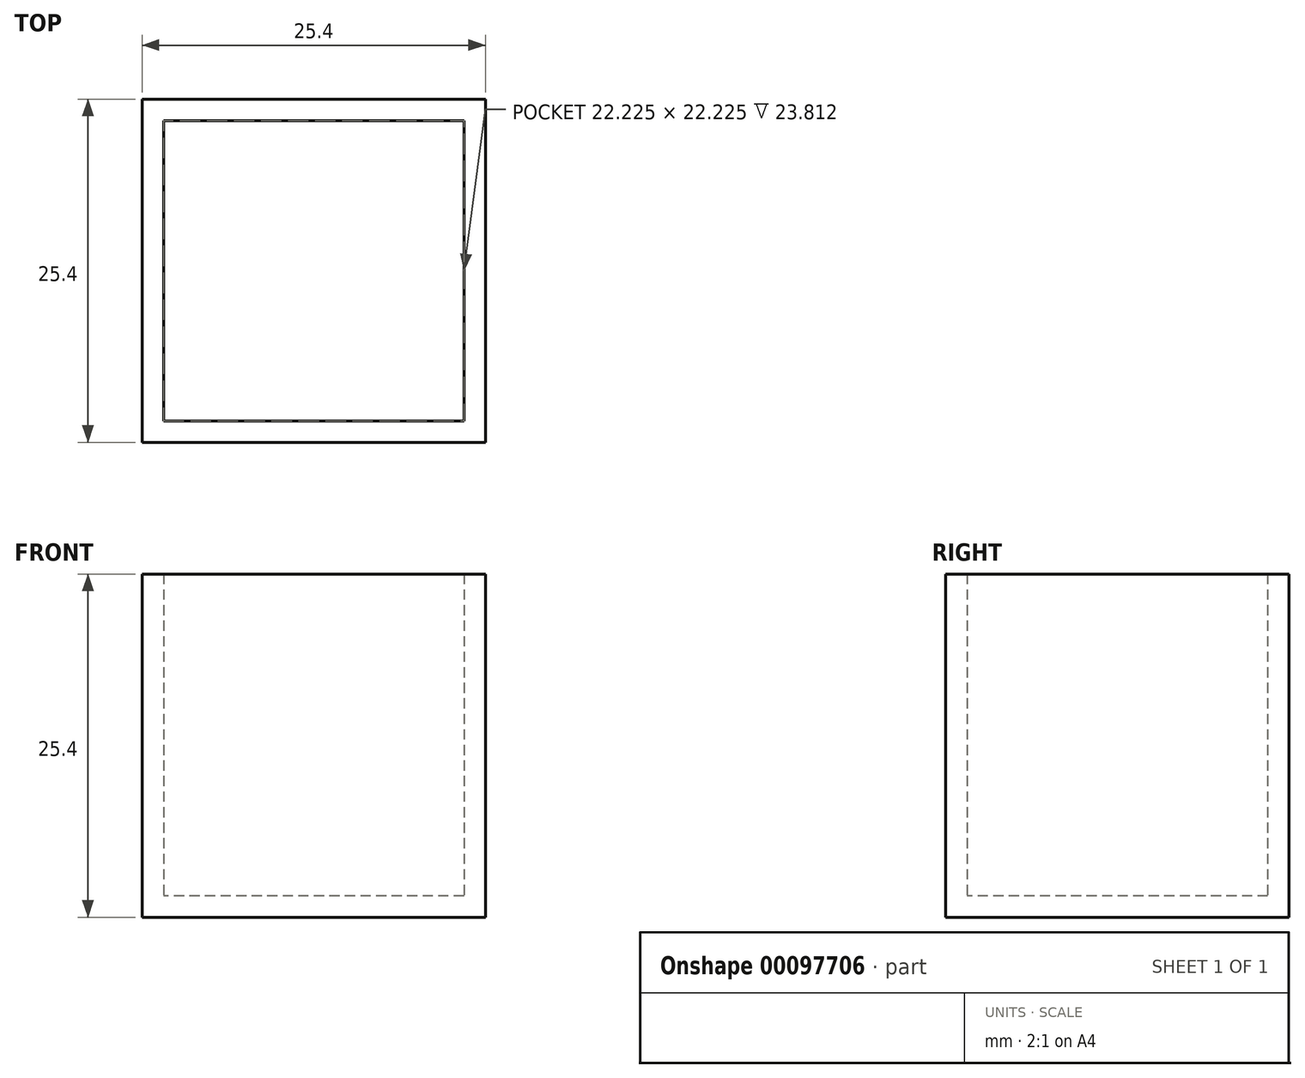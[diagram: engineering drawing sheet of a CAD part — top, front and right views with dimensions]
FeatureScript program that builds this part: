
annotation { "Feature Type Name" : "Feature", "Feature Type Description" : "" }
export const myFeature = defineFeature(function(context is Context, id is Id, definition is map)
    precondition{}
    {
        {
            var Q0;
            Q0=qCreatedBy(makeId("Top.planeOp"),FACE);
            var sketch = newSketch(context, id + "F0", { "sketchPlane" : qUnion([Q0])});
            skLineSegment(sketch, "E0.bottom", {"start": v(12.7, 12.7) * mm, "end": v(-12.7, 12.7) * mm});
            skLineSegment(sketch, "E0.top", {"start": v(12.7, -12.7) * mm, "end": v(-12.7, -12.7) * mm});
            skLineSegment(sketch, "E0.left", {"start": v(12.7, 12.7) * mm, "end": v(12.7, -12.7) * mm});
            skLineSegment(sketch, "E0.right", {"start": v(-12.7, 12.7) * mm, "end": v(-12.7, -12.7) * mm});
            skPoint(sketch, "E0.middle", {"position": v(0, 0) * mm});
            skSolve(sketch);
        }
        {
            var Q0;
            Q0 = qSketchRegion(id + "F0", true);
            extrude(context, id + "F1", {"entities" : qUnion([Q0]), "depth" : 1.59 * mm});
        }
        {
            var Q0;
            Q0=makeQuery(id+"F1.opExtrude","CAP_FACE",FACE,{"disambiguationData":[OSD([sQuery(id+"F0.wireOp",EDGE,"E0.bottom"),sQuery(id+"F0.wireOp",EDGE,"E0.top"),sQuery(id+"F0.wireOp",EDGE,"E0.left"),sQuery(id+"F0.wireOp",EDGE,"E0.right")])],"isStart":false});
            var sketch = newSketch(context, id + "F2", { "sketchPlane" : qUnion([Q0])});
            skLineSegment(sketch, "E1.bottom", {"start": v(11.11, 11.11) * mm, "end": v(-11.11, 11.11) * mm});
            skLineSegment(sketch, "E1.top", {"start": v(11.11, -11.11) * mm, "end": v(-11.11, -11.11) * mm});
            skLineSegment(sketch, "E1.left", {"start": v(11.11, 11.11) * mm, "end": v(11.11, -11.11) * mm});
            skLineSegment(sketch, "E1.right", {"start": v(-11.11, 11.11) * mm, "end": v(-11.11, -11.11) * mm});
            skPoint(sketch, "E1.middle", {"position": v(0, 0) * mm});
            skLineSegment(sketch, "E2.bottom", {"start": v(12.7, 12.7) * mm, "end": v(-12.7, 12.7) * mm});
            skLineSegment(sketch, "E2.top", {"start": v(12.7, -12.7) * mm, "end": v(-12.7, -12.7) * mm});
            skLineSegment(sketch, "E2.left", {"start": v(12.7, 12.7) * mm, "end": v(12.7, -12.7) * mm});
            skLineSegment(sketch, "E2.right", {"start": v(-12.7, 12.7) * mm, "end": v(-12.7, -12.7) * mm});
            skSolve(sketch);
        }
        {
            var Q0;
            Q0 = qSketchRegion(id + "F2", true);
            extrude(context, id + "F3", {"entities" : qUnion([Q0]), "operationType" : NewBodyOperationType.ADD, "depth" : 23.8 * mm});
        }
    });
